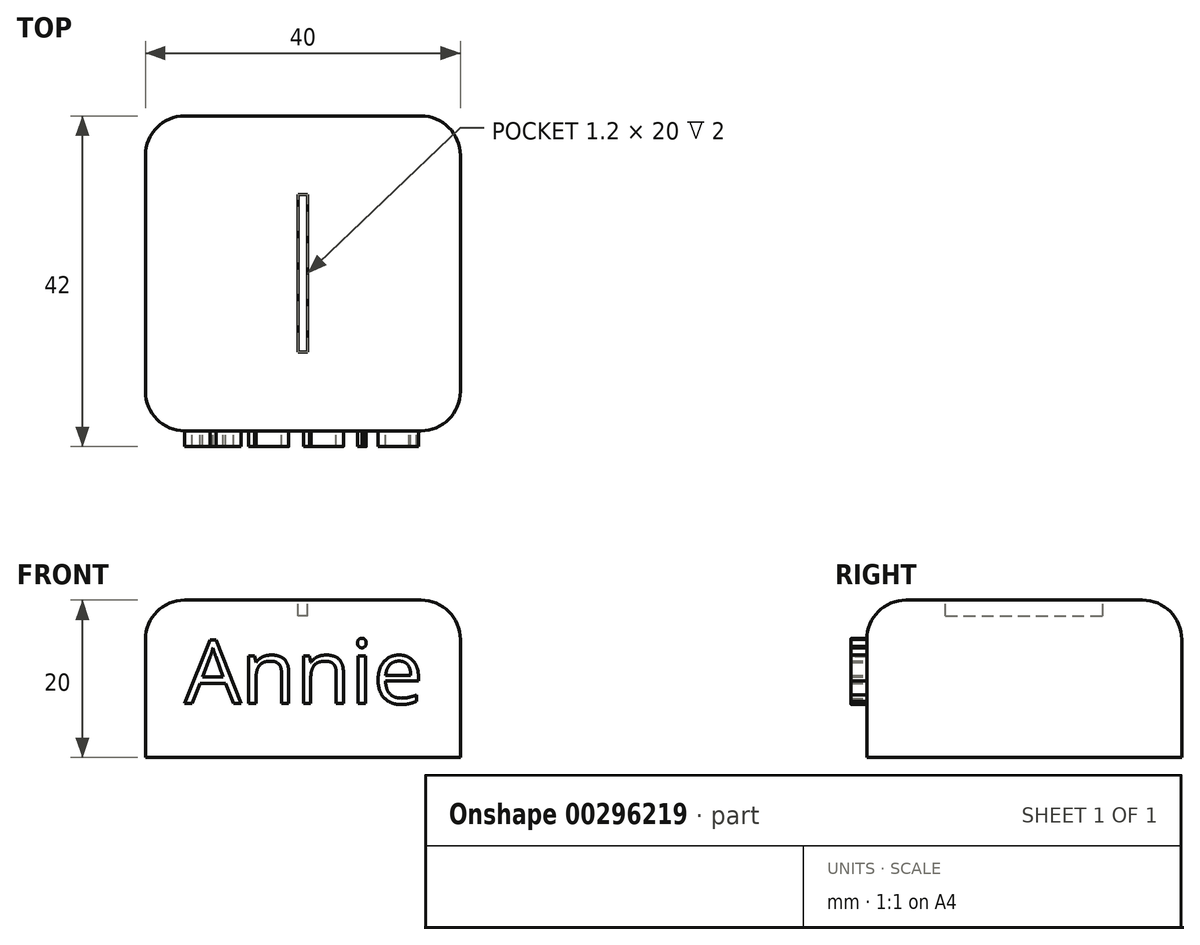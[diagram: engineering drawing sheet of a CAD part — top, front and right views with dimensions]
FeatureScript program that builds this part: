
annotation { "Feature Type Name" : "Feature", "Feature Type Description" : "" }
export const myFeature = defineFeature(function(context is Context, id is Id, definition is map)
    precondition{}
    {
        {
            var Q0;
            Q0=qCreatedBy(makeId("Top.planeOp"),FACE);
            var sketch = newSketch(context, id + "F0", { "sketchPlane" : qUnion([Q0])});
            skLineSegment(sketch, "E0.bottom", {"start": v(20, -20) * mm, "end": v(-20, -20) * mm});
            skLineSegment(sketch, "E0.top", {"start": v(20, 20) * mm, "end": v(-20, 20) * mm});
            skLineSegment(sketch, "E0.left", {"start": v(20, -20) * mm, "end": v(20, 20) * mm});
            skLineSegment(sketch, "E0.right", {"start": v(-20, -20) * mm, "end": v(-20, 20) * mm});
            skPoint(sketch, "E0.middle", {"position": v(0, 0) * mm});
            skLineSegment(sketch, "E1.bottom", {"start": v(0.6, -10) * mm, "end": v(-0.6, -10) * mm});
            skLineSegment(sketch, "E1.top", {"start": v(0.6, 10) * mm, "end": v(-0.6, 10) * mm});
            skLineSegment(sketch, "E1.left", {"start": v(0.6, -10) * mm, "end": v(0.6, 10) * mm});
            skLineSegment(sketch, "E1.right", {"start": v(-0.6, -10) * mm, "end": v(-0.6, 10) * mm});
            skSolve(sketch);
        }
        {
            var Q0;
            Q0=makeQuery(id+"F0.imprint","IMPRINT",FACE,{"disambiguationData":[TD([[makeQuery(id+"F0.imprint","IMPRINT",EDGE,{"derivedFrom":sQuery(id+"F0.wireOp",EDGE,"E0.bottom")}),-1.0]])]});
            var Q1;
            Q1=makeQuery(id+"F0.imprint","IMPRINT",FACE,{"disambiguationData":[TD([[makeQuery(id+"F0.imprint","IMPRINT",EDGE,{"derivedFrom":sQuery(id+"F0.wireOp",EDGE,"E1.bottom")}),-1.0]])]});
            extrude(context, id + "F1", {"entities" : qUnion([Q0, Q1]), "oppositeDirection" : true, "depth" : 20 * mm});
        }
        {
            var Q0;
            Q0=makeQuery(id+"F0.imprint","IMPRINT",FACE,{"disambiguationData":[TD([[makeQuery(id+"F0.imprint","IMPRINT",EDGE,{"derivedFrom":sQuery(id+"F0.wireOp",EDGE,"E1.bottom")}),-1.0]])]});
            extrude(context, id + "F2", {"entities" : qUnion([Q0]), "operationType" : NewBodyOperationType.REMOVE, "oppositeDirection" : true, "depth" : 2 * mm});
        }
        {
            var Q0;
            Q0=makeQuery(id+"F2.boolean.opBoolean","COPY",EDGE,{"derivedFrom":makeQuery(id+"F2.opExtrude","CAP_EDGE",EDGE,{"disambiguationData":[OSD([sQuery(id+"F0.wireOp",EDGE,"E1.left")])],"isStart":true})});
            var Q1;
            Q1=makeQuery(id+"F2.boolean.opBoolean","COPY",EDGE,{"derivedFrom":makeQuery(id+"F2.opExtrude","CAP_EDGE",EDGE,{"disambiguationData":[OSD([sQuery(id+"F0.wireOp",EDGE,"E1.right")])],"isStart":true})});
            var Q2;
            Q2=makeQuery(id+"F1.opExtrude","SWEPT_EDGE",EDGE,{"disambiguationData":[OSD([sQuery(id+"F0.wireOp",EDGE,"E0.bottom"),sQuery(id+"F0.wireOp",EDGE,"E0.left")])]});
            var Q3;
            Q3=makeQuery(id+"F1.opExtrude","SWEPT_EDGE",EDGE,{"disambiguationData":[OSD([sQuery(id+"F0.wireOp",EDGE,"E0.top"),sQuery(id+"F0.wireOp",EDGE,"E0.left")])]});
            var Q4;
            Q4=makeQuery(id+"F1.opExtrude","CAP_EDGE",EDGE,{"disambiguationData":[OSD([sQuery(id+"F0.wireOp",EDGE,"E0.left")])],"isStart":true});
            var Q5;
            Q5=makeQuery(id+"F1.opExtrude","SWEPT_EDGE",EDGE,{"disambiguationData":[OSD([sQuery(id+"F0.wireOp",EDGE,"E0.bottom"),sQuery(id+"F0.wireOp",EDGE,"E0.right")])]});
            var Q6;
            Q6=makeQuery(id+"F1.opExtrude","SWEPT_EDGE",EDGE,{"disambiguationData":[OSD([sQuery(id+"F0.wireOp",EDGE,"E0.top"),sQuery(id+"F0.wireOp",EDGE,"E0.right")])]});
            var Q7;
            Q7=makeQuery(id+"F1.opExtrude","CAP_EDGE",EDGE,{"disambiguationData":[OSD([sQuery(id+"F0.wireOp",EDGE,"E0.top")])],"isStart":true});
            var Q8;
            Q8=makeQuery(id+"F1.opExtrude","CAP_EDGE",EDGE,{"disambiguationData":[OSD([sQuery(id+"F0.wireOp",EDGE,"E0.right")])],"isStart":true});
            var Q9;
            Q9=makeQuery(id+"F1.opExtrude","CAP_EDGE",EDGE,{"disambiguationData":[OSD([sQuery(id+"F0.wireOp",EDGE,"E0.bottom")])],"isStart":true});
            fillet(context, id + "F3", {"entities" : qUnion([Q0, Q1, Q2, Q3, Q4, Q5, Q6, Q7, Q8, Q9]), "radius" : 5 * mm, "tangentPropagation" : true, "allowEdgeOverflow" : false});
        }
        {
            var Q0;
            Q0=makeQuery(id+"F1.opExtrude","SWEPT_FACE",FACE,{"disambiguationData":[OSD([sQuery(id+"F0.wireOp",EDGE,"E0.bottom")])]});
            var sketch = newSketch(context, id + "F4", { "sketchPlane" : qUnion([Q0])});
            skText(sketch, "E2", { "text": "Annie", "fontName": "OpenSans-Regular.ttf"});
            const initialGuessF4  = {"E2": [-0.015, -0.01315, 1, 0, 0.00815]};
            skSetInitialGuess(sketch, initialGuessF4);
            skSolve(sketch);
        }
        {
            var Q0;
            Q0=qSketchRegion(id+"F4",true);
            extrude(context, id + "F5", {"entities" : qUnion([Q0]), "operationType" : NewBodyOperationType.ADD, "depth" : 2 * mm});
        }
    });
